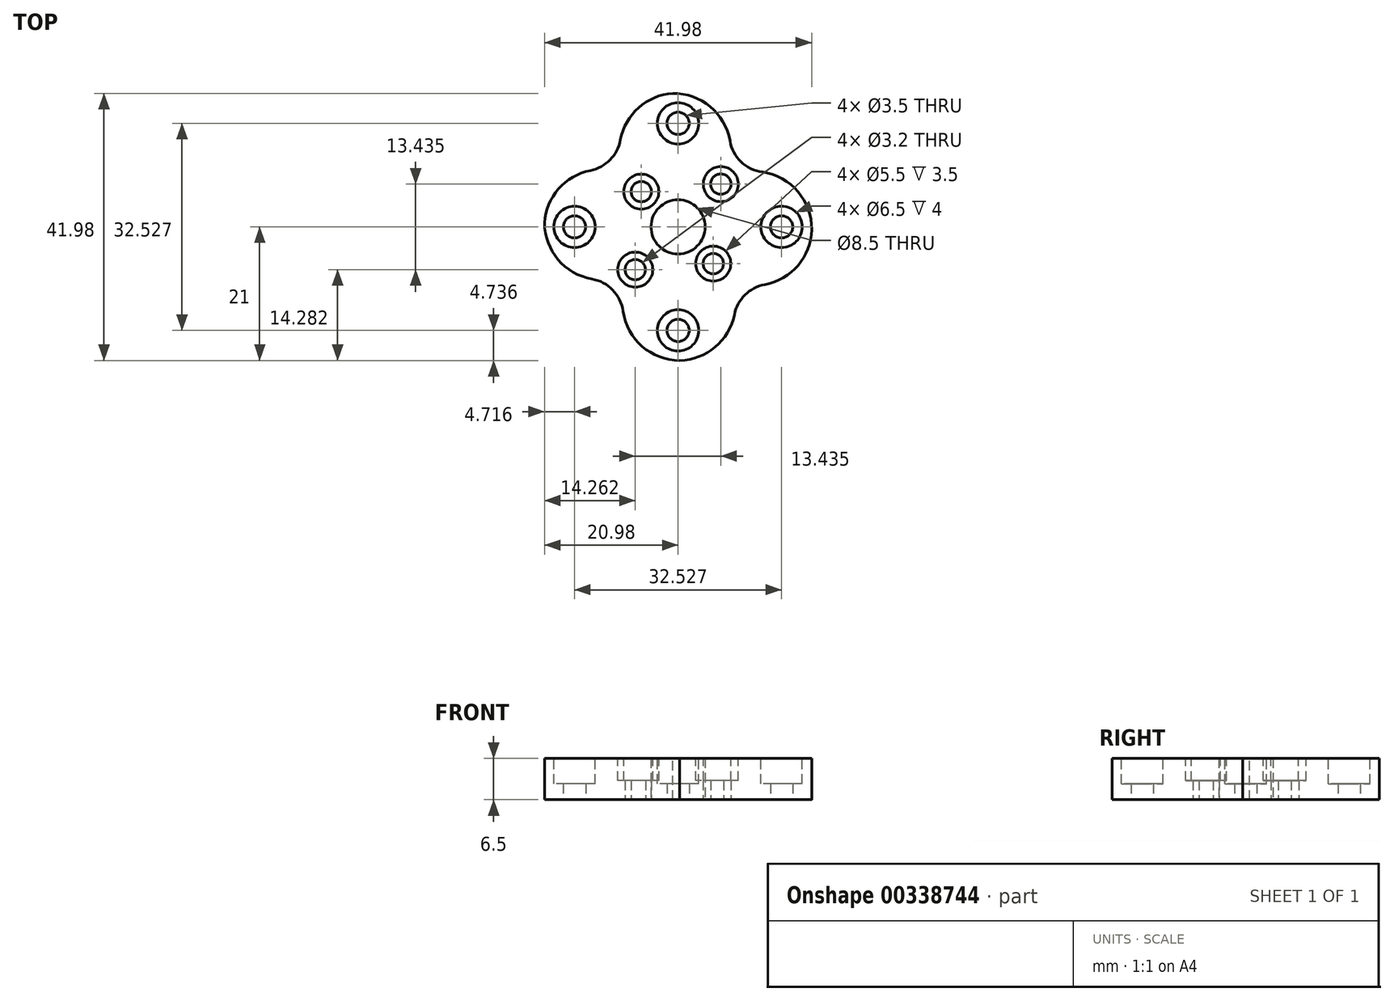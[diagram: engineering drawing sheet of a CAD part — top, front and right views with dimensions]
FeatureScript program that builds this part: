
annotation { "Feature Type Name" : "Feature", "Feature Type Description" : "" }
export const myFeature = defineFeature(function(context is Context, id is Id, definition is map)
    precondition{}
    {
        {
            assignVariable(context, id + "F0", {"name" : "thickness", "anyValue" : 6.5});
        }
        {
            assignVariable(context, id + "F1", {"name" : "screwHeadDepth", "anyValue" : 3.5});
        }
        {
            var Q0;
            Q0=qCreatedBy(makeId("Top.planeOp"),FACE);
            var sketch = newSketch(context, id + "F2", { "sketchPlane" : qUnion([Q0])});
            skCircle(sketch, "E0", {"center": v(0, 16.26) * mm, "radius": 1.75 * mm});
            skCircle(sketch, "E1", {"center": v(-16.26, 0) * mm, "radius": 1.75 * mm});
            skCircle(sketch, "E2", {"center": v(16.26, 0) * mm, "radius": 1.75 * mm});
            skCircle(sketch, "E3", {"center": v(0, -16.26) * mm, "radius": 1.75 * mm});
            skLineSegment(sketch, "E4", {"start": v(0, 0) * mm, "end": v(-16.26, 0) * mm});
            skLineSegment(sketch, "E5", {"start": v(0, 0) * mm, "end": v(0, 16.26) * mm});
            skLineSegment(sketch, "E6", {"start": v(0, 0) * mm, "end": v(16.26, 0) * mm});
            skLineSegment(sketch, "E7", {"start": v(0, 0) * mm, "end": v(0, -16.26) * mm});
            skCircle(sketch, "E8", {"center": v(0, 0) * mm, "radius": 4.25 * mm});
            skCircle(sketch, "E9", {"center": v(0, 0) * mm, "radius": 21 * mm});
            skLineSegment(sketch, "E10", {"start": v(-14.96, 14.73) * mm, "end": v(14.73, -14.96) * mm});
            skArc(sketch, "E11", {"start": v(18.36, -10.19) * mm, "mid": v(10.52, -10.69) * mm, "end": v(9.9, -18.52) * mm});
            skLineSegment(sketch, "E12", {"start": v(-14.85, -14.85) * mm, "end": v(14.85, 14.85) * mm});
            skCircle(sketch, "E13", {"center": v(-5.77, 5.54) * mm, "radius": 1.6 * mm});
            skCircle(sketch, "E14", {"center": v(6.72, 6.72) * mm, "radius": 1.6 * mm});
            skCircle(sketch, "E15", {"center": v(5.54, -5.77) * mm, "radius": 1.6 * mm});
            skCircle(sketch, "E16", {"center": v(-6.72, -6.72) * mm, "radius": 1.6 * mm});
            skCircle(sketch, "E17", {"center": v(-14.96, 14.73) * mm, "radius": 6 * mm});
            skCircle(sketch, "E18", {"center": v(-14.58, -14.1) * mm, "radius": 6 * mm});
            skCircle(sketch, "E19", {"center": v(14.06, 14.55) * mm, "radius": 6 * mm});
            skSolve(sketch);
        }
        {
            var Q0;
            {var subQ0=sQuery(id+"F2.wireOp",EDGE,"E5");var subQ1=sQuery(id+"F2.wireOp",EDGE,"E0");var subQ2=makeQuery(id+"F2.imprint","INTERSECT",VERTEX,{"derivedFrom":[subQ1,subQ0]});Q0=makeQuery(id+"F2.imprint","IMPRINT",FACE,{"disambiguationData":[TD([[makeQuery(id+"F2.imprint","IMPRINT",EDGE,{"disambiguationData":[TD([[subQ2,1.0]])],"derivedFrom":subQ1}),-1.0]])]});}
            var Q1;
            {var subQ7=sQuery(id+"F2.wireOp",EDGE,"E5");var subQ8=sQuery(id+"F2.wireOp",EDGE,"E0");var subQ9=makeQuery(id+"F2.imprint","INTERSECT",VERTEX,{"derivedFrom":[subQ8,subQ7]});Q1=makeQuery(id+"F2.imprint","IMPRINT",FACE,{"disambiguationData":[TD([[makeQuery(id+"F2.imprint","IMPRINT",EDGE,{"disambiguationData":[TD([[subQ9,-1.0]])],"derivedFrom":subQ8}),-1.0]])]});}
            var Q2;
            {var subQ5=sQuery(id+"F2.wireOp",EDGE,"E4");var subQ6=sQuery(id+"F2.wireOp",EDGE,"E1");var subQ7=makeQuery(id+"F2.imprint","INTERSECT",VERTEX,{"derivedFrom":[subQ6,subQ5]});Q2=makeQuery(id+"F2.imprint","IMPRINT",FACE,{"disambiguationData":[TD([[makeQuery(id+"F2.imprint","IMPRINT",EDGE,{"disambiguationData":[TD([[subQ7,1.0]])],"derivedFrom":subQ6}),-1.0]])]});}
            var Q3;
            {var subQ0=sQuery(id+"F2.wireOp",EDGE,"E6");var subQ1=sQuery(id+"F2.wireOp",EDGE,"E2");var subQ2=makeQuery(id+"F2.imprint","INTERSECT",VERTEX,{"derivedFrom":[subQ1,subQ0]});Q3=makeQuery(id+"F2.imprint","IMPRINT",FACE,{"disambiguationData":[TD([[makeQuery(id+"F2.imprint","IMPRINT",EDGE,{"disambiguationData":[TD([[subQ2,-1.0]])],"derivedFrom":subQ1}),-1.0]])]});}
            var Q4;
            Q4=makeQuery(id+"F2.imprint","IMPRINT",FACE,{"disambiguationData":[TD([[makeQuery(id+"F2.imprint","IMPRINT",EDGE,{"derivedFrom":sQuery(id+"F2.wireOp",EDGE,"E3")}),-1.0]])]});
            extrude(context, id + "F3", {"entities" : qUnion([Q0, Q1, Q2, Q3, Q4]), "depth" : (getVariable(context, 'thickness')) * mm});
        }
        {
            var Q0;
            Q0=makeQuery(id+"F3.opExtrude","CAP_FACE",FACE,{"disambiguationData":[OSD([sQuery(id+"F2.wireOp",EDGE,"E0"),sQuery(id+"F2.wireOp",EDGE,"E1"),sQuery(id+"F2.wireOp",EDGE,"E2"),sQuery(id+"F2.wireOp",EDGE,"E3"),sQuery(id+"F2.wireOp",EDGE,"E8"),sQuery(id+"F2.wireOp",EDGE,"E9"),sQuery(id+"F2.wireOp",EDGE,"E11"),sQuery(id+"F2.wireOp",EDGE,"E13"),sQuery(id+"F2.wireOp",EDGE,"E14"),sQuery(id+"F2.wireOp",EDGE,"E15"),sQuery(id+"F2.wireOp",EDGE,"E16")])],"isStart":false});
            var sketch = newSketch(context, id + "F4", { "sketchPlane" : qUnion([Q0])});
            skCircle(sketch, "E20", {"center": v(-5.77, 5.54) * mm, "radius": 2.75 * mm});
            skCircle(sketch, "E21", {"center": v(5.54, -5.77) * mm, "radius": 2.75 * mm});
            skCircle(sketch, "E22", {"center": v(-6.72, -6.72) * mm, "radius": 2.75 * mm});
            skCircle(sketch, "E23", {"center": v(6.72, 6.72) * mm, "radius": 2.75 * mm});
            skSolve(sketch);
        }
        {
            var Q0;
            Q0 = qSketchRegion(id + "F4", true);
            extrude(context, id + "F5", {"entities" : qUnion([Q0]), "operationType" : NewBodyOperationType.REMOVE, "oppositeDirection" : true, "depth" : (getVariable(context, 'screwHeadDepth')) * mm});
        }
        {
            var Q0;
            {var subQ0=sQuery(id+"F2.wireOp",EDGE,"E17");var subQ1=sQuery(id+"F2.wireOp",EDGE,"E9");Q0=makeQuery(id+"F3.opExtrude","SWEPT_EDGE",EDGE,{"disambiguationData":[OSD([subQ1,subQ0]),TDD([makeQuery(id+"F2.imprint","INTERSECT",VERTEX,{"disambiguationData":[OD(0.0)],"derivedFrom":[subQ1,subQ0]})])]});}
            var Q1;
            {var subQ0=sQuery(id+"F2.wireOp",EDGE,"E19");var subQ1=sQuery(id+"F2.wireOp",EDGE,"E9");Q1=makeQuery(id+"F3.opExtrude","SWEPT_EDGE",EDGE,{"disambiguationData":[OSD([subQ1,subQ0]),TDD([makeQuery(id+"F2.imprint","INTERSECT",VERTEX,{"disambiguationData":[OD(1.0)],"derivedFrom":[subQ1,subQ0]})])]});}
            var Q2;
            {var subQ0=sQuery(id+"F2.wireOp",EDGE,"E19");var subQ1=sQuery(id+"F2.wireOp",EDGE,"E9");Q2=makeQuery(id+"F3.opExtrude","SWEPT_EDGE",EDGE,{"disambiguationData":[OSD([subQ1,subQ0]),TDD([makeQuery(id+"F2.imprint","INTERSECT",VERTEX,{"disambiguationData":[OD(0.0)],"derivedFrom":[subQ1,subQ0]})])]});}
            var Q3;
            {var subQ0=sQuery(id+"F2.wireOp",EDGE,"E11");var subQ1=sQuery(id+"F2.wireOp",EDGE,"E9");Q3=makeQuery(id+"F3.opExtrude","SWEPT_EDGE",EDGE,{"disambiguationData":[OSD([subQ1,subQ0]),TDD([makeQuery(id+"F2.imprint","INTERSECT",VERTEX,{"disambiguationData":[OD(0.0)],"derivedFrom":[subQ1,subQ0]})])]});}
            var Q4;
            {var subQ0=sQuery(id+"F2.wireOp",EDGE,"E11");var subQ1=sQuery(id+"F2.wireOp",EDGE,"E9");Q4=makeQuery(id+"F3.opExtrude","SWEPT_EDGE",EDGE,{"disambiguationData":[OSD([subQ1,subQ0]),TDD([makeQuery(id+"F2.imprint","INTERSECT",VERTEX,{"disambiguationData":[OD(1.0)],"derivedFrom":[subQ1,subQ0]})])]});}
            var Q5;
            {var subQ0=sQuery(id+"F2.wireOp",EDGE,"E18");var subQ1=sQuery(id+"F2.wireOp",EDGE,"E9");Q5=makeQuery(id+"F3.opExtrude","SWEPT_EDGE",EDGE,{"disambiguationData":[OSD([subQ1,subQ0]),TDD([makeQuery(id+"F2.imprint","INTERSECT",VERTEX,{"disambiguationData":[OD(1.0)],"derivedFrom":[subQ1,subQ0]})])]});}
            var Q6;
            {var subQ0=sQuery(id+"F2.wireOp",EDGE,"E18");var subQ1=sQuery(id+"F2.wireOp",EDGE,"E9");Q6=makeQuery(id+"F3.opExtrude","SWEPT_EDGE",EDGE,{"disambiguationData":[OSD([subQ1,subQ0]),TDD([makeQuery(id+"F2.imprint","INTERSECT",VERTEX,{"disambiguationData":[OD(0.0)],"derivedFrom":[subQ1,subQ0]})])]});}
            var Q7;
            {var subQ0=sQuery(id+"F2.wireOp",EDGE,"E17");var subQ1=sQuery(id+"F2.wireOp",EDGE,"E9");Q7=makeQuery(id+"F3.opExtrude","SWEPT_EDGE",EDGE,{"disambiguationData":[OSD([subQ1,subQ0]),TDD([makeQuery(id+"F2.imprint","INTERSECT",VERTEX,{"disambiguationData":[OD(1.0)],"derivedFrom":[subQ1,subQ0]})])]});}
            fillet(context, id + "F6", {"entities" : qUnion([Q0, Q1, Q2, Q3, Q4, Q5, Q6, Q7]), "radius" : 9 * mm, "tangentPropagation" : true, "allowEdgeOverflow" : false});
        }
        {
            var Q0;
            Q0=makeQuery(id+"F3.opExtrude","CAP_FACE",FACE,{"disambiguationData":[OSD([sQuery(id+"F2.wireOp",EDGE,"E0"),sQuery(id+"F2.wireOp",EDGE,"E1"),sQuery(id+"F2.wireOp",EDGE,"E2"),sQuery(id+"F2.wireOp",EDGE,"E3"),sQuery(id+"F2.wireOp",EDGE,"E8"),sQuery(id+"F2.wireOp",EDGE,"E9"),sQuery(id+"F2.wireOp",EDGE,"E11"),sQuery(id+"F2.wireOp",EDGE,"E13"),sQuery(id+"F2.wireOp",EDGE,"E14"),sQuery(id+"F2.wireOp",EDGE,"E15"),sQuery(id+"F2.wireOp",EDGE,"E16"),sQuery(id+"F2.wireOp",EDGE,"E17"),sQuery(id+"F2.wireOp",EDGE,"E18"),sQuery(id+"F2.wireOp",EDGE,"E19")])],"isStart":false});
            var sketch = newSketch(context, id + "F7", { "sketchPlane" : qUnion([Q0])});
            skCircle(sketch, "E24", {"center": v(-16.26, 0) * mm, "radius": 3.25 * mm});
            skCircle(sketch, "E25", {"center": v(0, 16.26) * mm, "radius": 3.25 * mm});
            skCircle(sketch, "E26", {"center": v(16.26, 0) * mm, "radius": 3.25 * mm});
            skCircle(sketch, "E27", {"center": v(0, -16.26) * mm, "radius": 3.25 * mm});
            skSolve(sketch);
        }
        {
            var Q0;
            Q0 = qSketchRegion(id + "F7", true);
            extrude(context, id + "F8", {"entities" : qUnion([Q0]), "operationType" : NewBodyOperationType.REMOVE, "oppositeDirection" : true, "depth" : 4 * mm});
        }
    });
